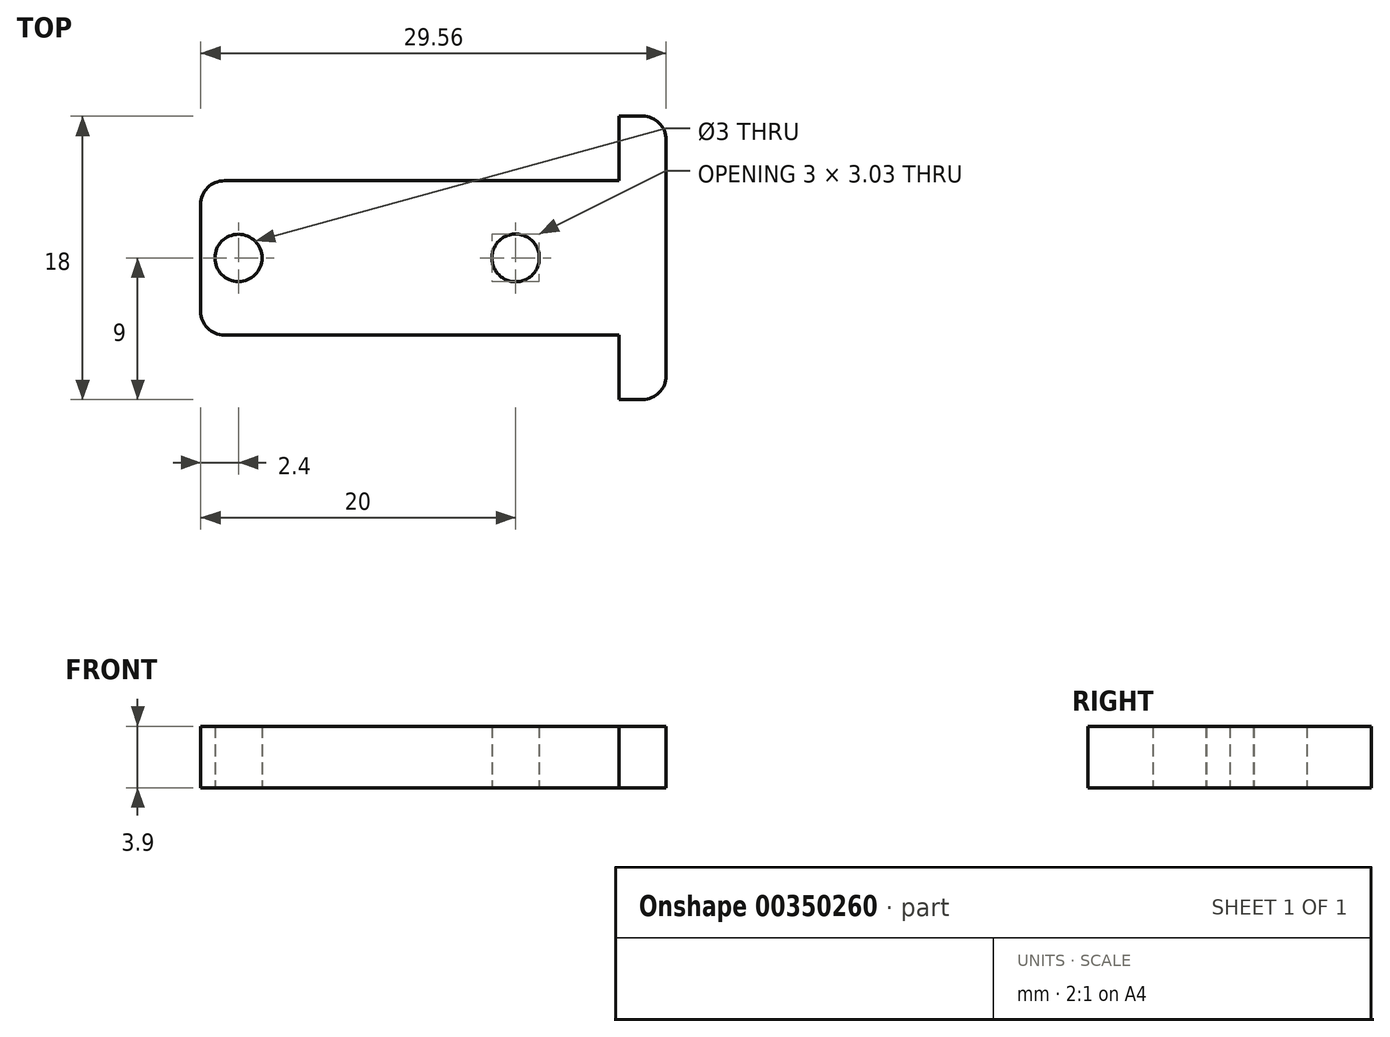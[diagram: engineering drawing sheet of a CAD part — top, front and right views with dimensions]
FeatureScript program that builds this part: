
annotation { "Feature Type Name" : "Feature", "Feature Type Description" : "" }
export const myFeature = defineFeature(function(context is Context, id is Id, definition is map)
    precondition{}
    {
        {
            var Q0;
            Q0=qCreatedBy(makeId("Top.planeOp"),FACE);
            var sketch = newSketch(context, id + "F0", { "sketchPlane" : qUnion([Q0])});
            skLineSegment(sketch, "E0", {"start": v(0, 0) * mm, "end": v(0, 3.4) * mm});
            skLineSegment(sketch, "E1", {"start": v(1.5, 4.9) * mm, "end": v(26.56, 4.9) * mm});
            skLineSegment(sketch, "E2", {"start": v(26.56, 4.9) * mm, "end": v(26.56, 9) * mm});
            skLineSegment(sketch, "E3", {"start": v(26.56, 9) * mm, "end": v(28.06, 9) * mm});
            skLineSegment(sketch, "E4", {"start": v(29.56, 7.5) * mm, "end": v(29.56, 0) * mm});
            skCircle(sketch, "E5", {"center": v(2.4, 0) * mm, "radius": 1.5 * mm});
            skCircle(sketch, "E6", {"center": v(20, -0.02) * mm, "radius": 1.5 * mm});
            skPoint(sketch, "E7.visualSharp", {"position": v(0, 4.9) * mm});
            skArc(sketch, "E7.filletArc", {"start": v(1.5, 4.9) * mm, "mid": v(0.44, 4.46) * mm, "end": v(0, 3.4) * mm});
            skPoint(sketch, "E8.visualSharp", {"position": v(29.56, 9) * mm});
            skArc(sketch, "E8.filletArc", {"start": v(29.56, 7.5) * mm, "mid": v(29.12, 8.56) * mm, "end": v(28.06, 9) * mm});
            skLineSegment(sketch, "E9.MirrorCS", {"start": v(26.56, -9) * mm, "end": v(28.06, -9) * mm});
            skArc(sketch, "E10.MirrorCS", {"start": v(1.5, -4.9) * mm, "mid": v(0.44, -4.46) * mm, "end": v(0, -3.4) * mm});
            skArc(sketch, "E11.MirrorCS", {"start": v(29.56, -7.5) * mm, "mid": v(29.12, -8.56) * mm, "end": v(28.06, -9) * mm});
            skPoint(sketch, "E12.MirrorP", {"position": v(0, -4.9) * mm});
            skCircle(sketch, "E13.MirrorC", {"center": v(20, 0.02) * mm, "radius": 1.5 * mm});
            skLineSegment(sketch, "E14.MirrorCS", {"start": v(0, 0) * mm, "end": v(0, -3.4) * mm});
            skLineSegment(sketch, "E15.MirrorCS", {"start": v(29.56, -7.5) * mm, "end": v(29.56, 0) * mm});
            skPoint(sketch, "E16.MirrorP", {"position": v(29.56, -9) * mm});
            skLineSegment(sketch, "E17.MirrorCS", {"start": v(26.56, -4.9) * mm, "end": v(26.56, -9) * mm});
            skLineSegment(sketch, "E18.MirrorCS", {"start": v(1.5, -4.9) * mm, "end": v(26.56, -4.9) * mm});
            skSolve(sketch);
        }
        {
            var Q0;
            Q0 = qSketchRegion(id + "F0", true);
            extrude(context, id + "F1", {"entities" : qUnion([Q0]), "depth" : 3.9 * mm});
        }
    });
